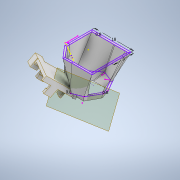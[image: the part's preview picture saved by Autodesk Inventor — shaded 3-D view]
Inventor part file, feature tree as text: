
AUTODESK INVENTOR PART (.ipt)
format: ipt  version: 2022 (Build 260153000, 153)  size: 494,080 bytes
history: native  units: in
note: dims shown in document units (in); Inventor stores cm internally (conversion verified against a paired STEP export)
features: sketch x8, plane x5, loft x5, other x3, extrude x1, split x1, move_body x1
ambient origin geometry x8: Origin, YZ Plane, XZ Plane, XY Plane, X Axis, Y Axis, Z Axis, Center Point
bodies: Solid1 (feature_tree)
feature tree (24):
  sketch  "Sketch1"  dims[d0=0.2441in d1=60.0deg]
  plane  "Work Plane1"
  plane  "Work Plane2"
  sketch  "Sketch2"  dims[d2=0.1063in d3=0.202in]
  extrude  "Extrusion3"  TaperAngle=60.0deg  [1 undecoded]
  plane  "Work Plane5"
  sketch  "Sketch4"  dims[d8=0.0315in d11=0.1181in]
  plane  "Work Plane3"
  split  "Split3"
  sketch  "Sketch5"  dims[d14=0.0315in d15=0.0315in]
  plane  "Work Plane4"
  sketch  "Sketch6"  dims[d20=0.1181in d27=0.1181in d28=0.1181in d29=0.0in d30=0.0in]
  loft  "Loft3"
  loft  "Loft4"
  other  "cam_holder_new_module"
  sketch  "Sketch7"  dims[d33=0.3937in]
  loft  "Loft5"
  move_body  "Move Body3"
  loft  "Loft7"
  loft  "Loft8"
  sketch  "Sketch3"  dims[d4=0.1181in d7=0.0315in]
  sketch  "Sketch8"  dims[d36=0.0315in d40=0.6299in d44=0.3543in d45=0.7087in d48=0.0315in d57=0.0in d58=90.0deg d59=0.0in d60=90.0deg d61=0.0in d62=90.0deg d63=0.0in d64=90.0deg d73=0.0933in d74=0.0315in d75=0.0984in d76=0.0591in d77=0.0591in d78=0.0in d79=90.0deg d80=0.0in d81=90.0deg d84=30.0deg d88=-0.3436in d89=-0.3125in d90=0.0394in d91=-0.1535in d96=0.0in d97=90.0deg d98=0.0in d99=90.0deg d100=0.0in d101=90.0deg d102=0.0in d103=90.0deg]
  other  "Composite1"
  other  "Srf1"
note: 1 required parameter value undecoded (feature->parameter linkage not recoverable at this tier; creation-order binding heuristic only, values carry confidence <= 0.55)
